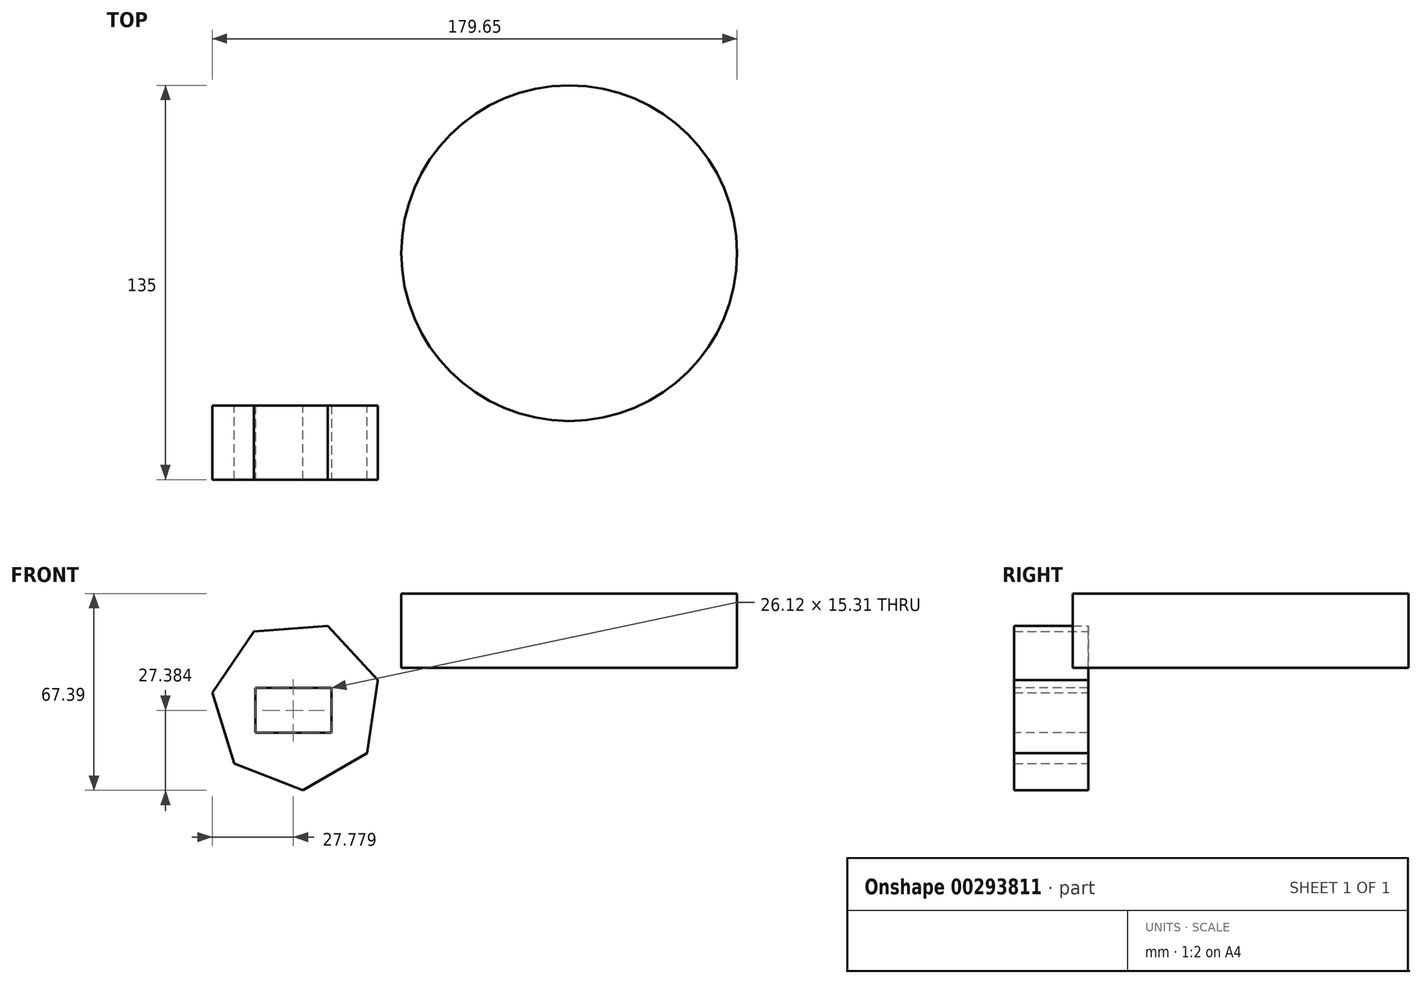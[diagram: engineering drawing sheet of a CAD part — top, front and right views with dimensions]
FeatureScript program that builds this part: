
annotation { "Feature Type Name" : "Feature", "Feature Type Description" : "" }
export const myFeature = defineFeature(function(context is Context, id is Id, definition is map)
    precondition{}
    {
        {
            var Q0;
            Q0=qCreatedBy(makeId("Front.planeOp"),FACE);
            var sketch = newSketch(context, id + "F0", { "sketchPlane" : qUnion([Q0])});
            skLineSegment(sketch, "E0.bottom", {"start": v(-41.4, 15.65) * mm, "end": v(57.4, 15.65) * mm});
            skLineSegment(sketch, "E0.top", {"start": v(-41.4, 39.09) * mm, "end": v(57.4, 39.09) * mm});
            skLineSegment(sketch, "E0.left", {"start": v(-41.4, 15.65) * mm, "end": v(-41.4, 39.09) * mm});
            skLineSegment(sketch, "E0.right", {"start": v(57.4, 15.65) * mm, "end": v(57.4, 39.09) * mm});
            skCircle(sketch, "E1.cCircle", {"center": v(-77.37, -12.9) * mm, "radius": 26.3 * mm, "construction": true});
            skLineSegment(sketch, "E1.0", {"start": v(-66.74, 14.29) * mm, "end": v(-49.5, -4.25) * mm});
            skLineSegment(sketch, "E1.1", {"start": v(-49.5, -4.25) * mm, "end": v(-53.24, -29.3) * mm});
            skLineSegment(sketch, "E1.2", {"start": v(-53.24, -29.3) * mm, "end": v(-75.15, -41.99) * mm});
            skLineSegment(sketch, "E1.3", {"start": v(-75.15, -41.99) * mm, "end": v(-98.73, -32.77) * mm});
            skLineSegment(sketch, "E1.4", {"start": v(-98.73, -32.77) * mm, "end": v(-106.23, -8.58) * mm});
            skLineSegment(sketch, "E1.5", {"start": v(-106.23, -8.58) * mm, "end": v(-92, 12.36) * mm});
            skLineSegment(sketch, "E1.6", {"start": v(-92, 12.36) * mm, "end": v(-66.74, 14.29) * mm});
            skPoint(sketch, "E1.0.midPoint", {"position": v(-58.12, 5.02) * mm});
            skSolve(sketch);
        }
        {
            var Q0;
            Q0=makeQuery(id+"F0.imprint","IMPRINT",FACE,{"disambiguationData":[TD([[makeQuery(id+"F0.imprint","IMPRINT",EDGE,{"derivedFrom":sQuery(id+"F0.wireOp",EDGE,"E1.0")}),-1.0]])]});
            extrude(context, id + "F1", {"entities" : qUnion([Q0]), "depth" : 25.4 * mm});
        }
        {
            var Q0;
            Q0=makeQuery(id+"F1.opExtrude","CAP_FACE",FACE,{"disambiguationData":[OSD([sQuery(id+"F0.wireOp",EDGE,"E1.0"),sQuery(id+"F0.wireOp",EDGE,"E1.1"),sQuery(id+"F0.wireOp",EDGE,"E1.2"),sQuery(id+"F0.wireOp",EDGE,"E1.3"),sQuery(id+"F0.wireOp",EDGE,"E1.4"),sQuery(id+"F0.wireOp",EDGE,"E1.5"),sQuery(id+"F0.wireOp",EDGE,"E1.6")])],"isStart":false});
            var sketch = newSketch(context, id + "F2", { "sketchPlane" : qUnion([Q0])});
            skLineSegment(sketch, "E2.bottom", {"start": v(-91.51, -6.95) * mm, "end": v(-65.4, -6.95) * mm});
            skLineSegment(sketch, "E2.top", {"start": v(-91.51, -22.26) * mm, "end": v(-65.4, -22.26) * mm});
            skLineSegment(sketch, "E2.left", {"start": v(-91.51, -6.95) * mm, "end": v(-91.51, -22.26) * mm});
            skLineSegment(sketch, "E2.right", {"start": v(-65.4, -6.95) * mm, "end": v(-65.4, -22.26) * mm});
            skSolve(sketch);
        }
        {
            var Q0;
            Q0=makeQuery(id+"F2.imprint","IMPRINT",FACE,{"disambiguationData":[TD([[makeQuery(id+"F2.imprint","IMPRINT",EDGE,{"derivedFrom":sQuery(id+"F2.wireOp",EDGE,"E2.bottom")}),-1.0]])]});
            extrude(context, id + "F3", {"entities" : qUnion([Q0]), "operationType" : NewBodyOperationType.REMOVE, "endBound" : BoundingType.THROUGH_ALL, "oppositeDirection" : true, "depth" : 25.4 * mm});
        }
        {
            var Q0;
            Q0=qCreatedBy(makeId("Top.planeOp"),FACE);
            var sketch = newSketch(context, id + "F4", { "sketchPlane" : qUnion([Q0])});
            skCircle(sketch, "E3", {"center": v(15.95, 52.13) * mm, "radius": 57.47 * mm});
            skSolve(sketch);
        }
        {
            var Q0;
            Q0=makeQuery(id+"F4.imprint","IMPRINT",FACE,{"disambiguationData":[TD([[makeQuery(id+"F4.imprint","IMPRINT",EDGE,{"derivedFrom":sQuery(id+"F4.wireOp",EDGE,"E3")}),1.0]])]});
            extrude(context, id + "F5", {"entities" : qUnion([Q0]), "depth" : 25.4 * mm});
        }
    });
